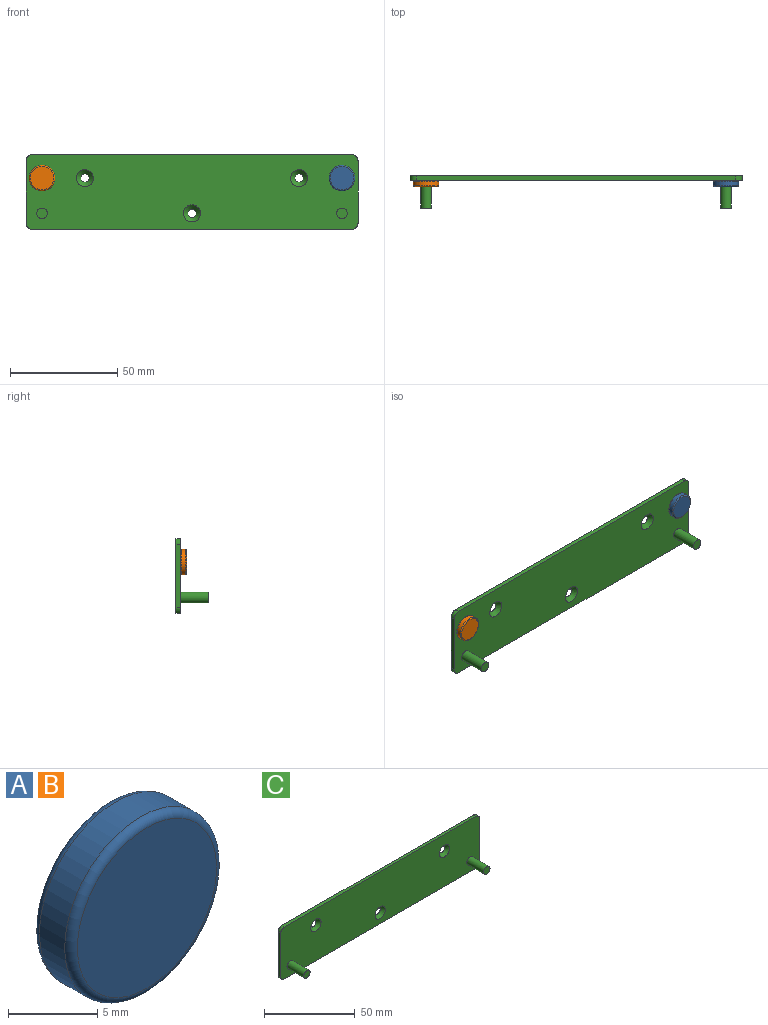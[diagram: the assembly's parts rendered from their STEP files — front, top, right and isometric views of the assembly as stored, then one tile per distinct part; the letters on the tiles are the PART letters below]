
ASSEMBLY  parts=3 mates=2
PART A: 5 faces, bbox 13x3x13 mm
  f0: cylinder r=6mm len=12mm, axis (0,-1,0), area 75.4mm2, adj f3,f4
  f1: plane 11x11mm, normal (0,1,0), area 95mm2, adj f4
  f2: plane 11x11mm, normal (0,-1,0), area 95mm2, adj f3
  f3: torus R=5.5mm, axis (0,1,0), area 28.7mm2, adj f0,f2
  f4: torus R=5.5mm, axis (0,1,0), area 28.7mm2, adj f0,f1
PART B: same geometry as A
PART C: 17 faces, bbox 155x15x35 mm
  f0: plane 149x2mm, normal (0,0,1), area 298mm2, adj f1,f7,f8,f9
  f1: cylinder r=3mm len=3mm, axis (0,1,0), area 9.4mm2, adj f0,f2,f8,f9
  f2: plane 29x2mm, normal (1,0,0), area 58mm2, adj f1,f3,f8,f9
  f3: cylinder r=3mm len=3mm, axis (0,1,0), area 9.4mm2, adj f2,f4,f8,f9
  f4: plane 149x2mm, normal (0,0,-1), area 298mm2, adj f3,f5,f8,f9
  f5: cylinder r=3mm len=3mm, axis (0,1,0), area 9.4mm2, adj f4,f6,f8,f9
  f6: plane 29x2mm, normal (-1,0,0), area 58mm2, adj f5,f7,f8,f9
  f7: cylinder r=3mm len=3mm, axis (0,1,0), area 9.4mm2, adj f0,f6,f8,f9
  f8: plane 155x35mm, normal (0,-1,0), area 5227.2mm2, adj f0,f1,f2,f3,f4,f5,f6,f7
  f9: plane 155x35mm, normal (0,1,0), area 5379.6mm2, adj f0,f1,f2,f3,f4,f5,f6,f7
  f10: cylinder r=2.5mm len=13mm, axis (0,1,0), area 204.2mm2, adj f8,f11
  f11: plane 5x5mm, normal (0,-1,0), area 19.6mm2, adj f10
  f12: cylinder r=2.5mm len=13mm, axis (0,1,0), area 204.2mm2, adj f8,f13
  f13: plane 5x5mm, normal (0,-1,0), area 19.6mm2, adj f12
  f14: cone r=4mm half-angle=45deg, axis (0,-1,0), area 53.3mm2, adj f8,f9
  f15: cone r=4mm half-angle=45deg, axis (0,-1,0), area 53.3mm2, adj f8,f9
  f16: cone r=2mm half-angle=45deg, axis (0,-1,0), area 53.3mm2, adj f8,f9
PLACE A t=(0,-5,0)mm
PLACE B t=(-140,-5,0)mm
PLACE C at identity
MATE fastened B.f0 <-> C.f8  axis (0,1,0) through (-70,18,0)mm
MATE fastened A.f0 <-> C.f8  axis (0,1,0) through (70,18,0)mm
